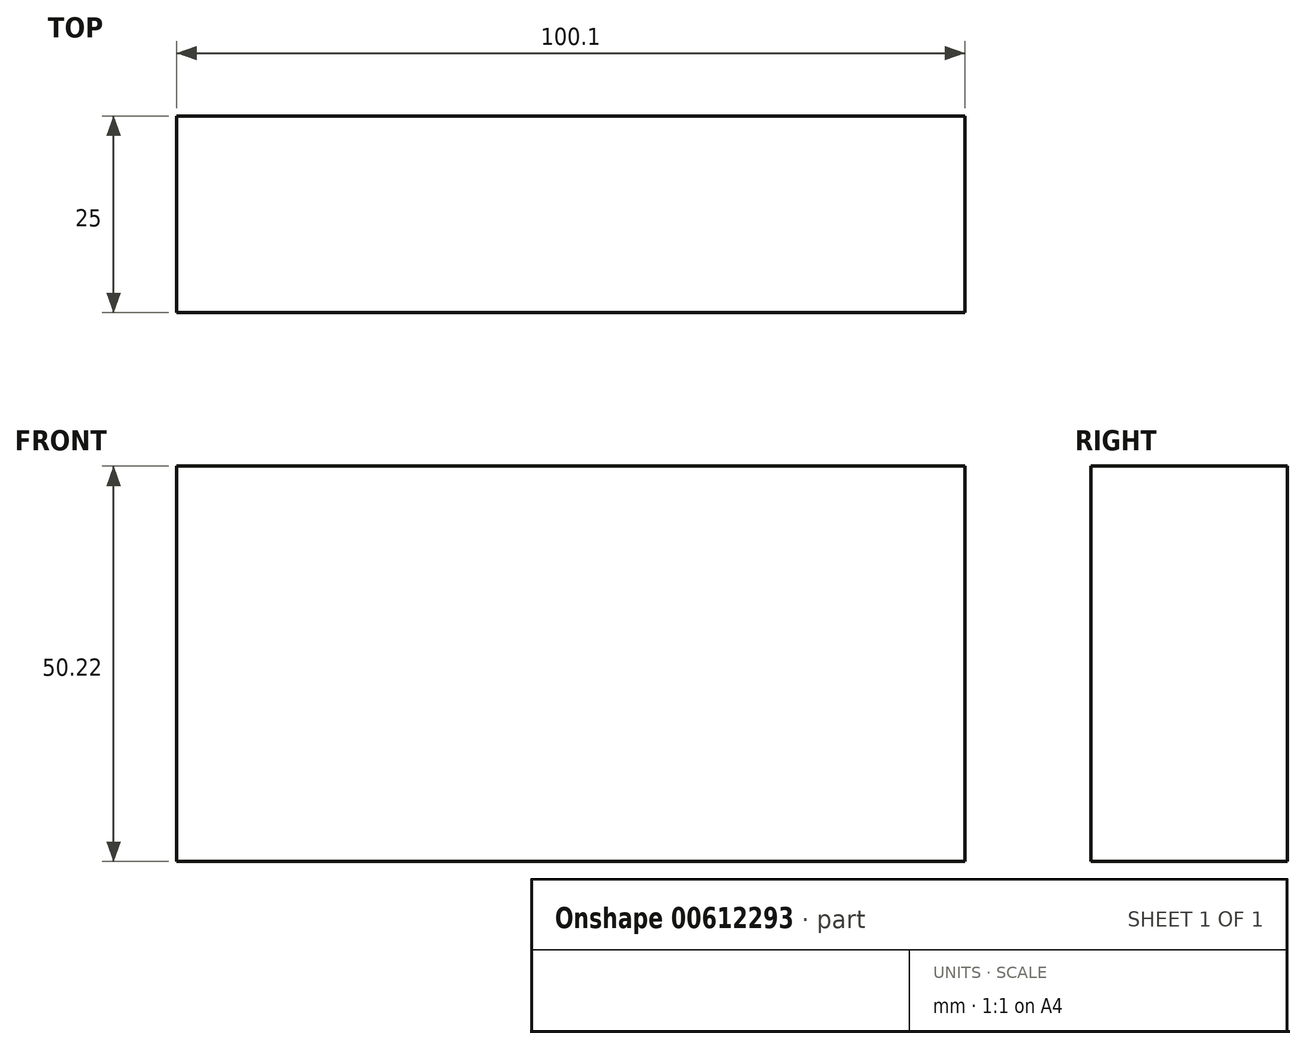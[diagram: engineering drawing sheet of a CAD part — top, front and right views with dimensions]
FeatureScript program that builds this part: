
annotation { "Feature Type Name" : "Feature", "Feature Type Description" : "" }
export const myFeature = defineFeature(function(context is Context, id is Id, definition is map)
    precondition{}
    {
        {
            var Q0;
            Q0=qCreatedBy(makeId("Front.planeOp"),FACE);
            var sketch = newSketch(context, id + "F0", { "sketchPlane" : qUnion([Q0])});
            skLineSegment(sketch, "E0.bottom", {"start": v(-60.11, 42.26) * mm, "end": v(39.99, 42.26) * mm});
            skLineSegment(sketch, "E0.top", {"start": v(-60.11, -7.96) * mm, "end": v(39.99, -7.96) * mm});
            skLineSegment(sketch, "E0.left", {"start": v(-60.11, 42.26) * mm, "end": v(-60.11, -7.96) * mm});
            skLineSegment(sketch, "E0.right", {"start": v(39.99, 42.26) * mm, "end": v(39.99, -7.96) * mm});
            skSolve(sketch);
        }
        {
            var Q0;
            Q0=makeQuery(id+"F0.imprint","IMPRINT",FACE,{"disambiguationData":[TD([[makeQuery(id+"F0.imprint","IMPRINT",EDGE,{"derivedFrom":sQuery(id+"F0.wireOp",EDGE,"E0.bottom")}),-1.0]])]});
            extrude(context, id + "F1", {"entities" : qUnion([Q0]), "depth" : 25 * mm, "offsetDistance" : 25 * mm});
        }
    });
